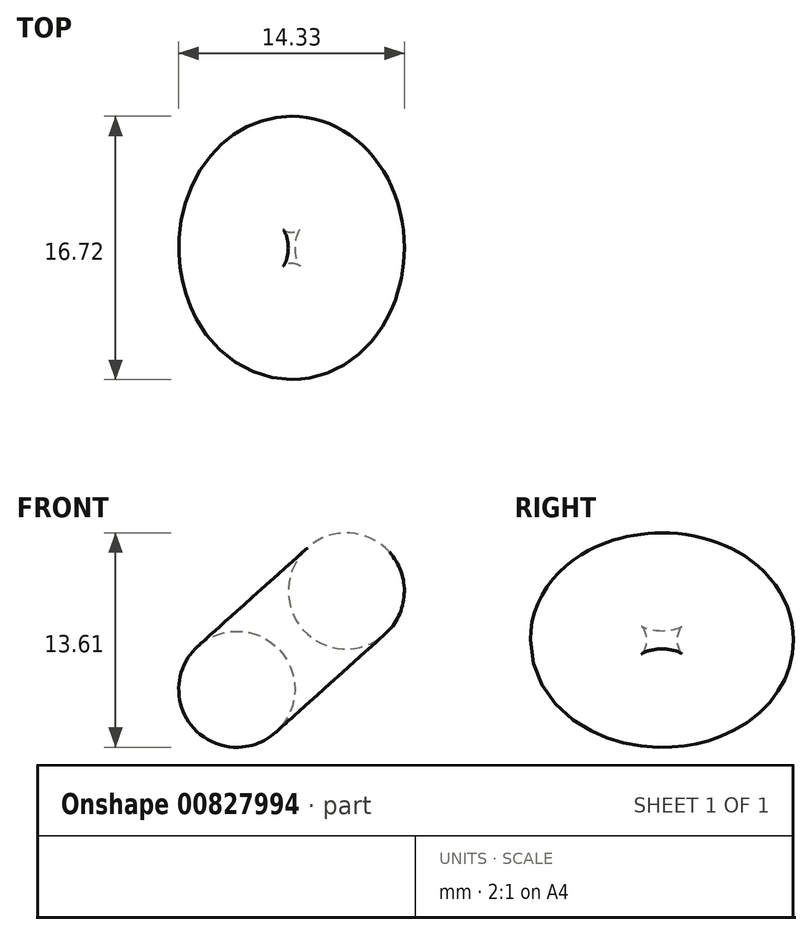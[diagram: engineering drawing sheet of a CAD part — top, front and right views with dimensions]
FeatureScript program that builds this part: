
annotation { "Feature Type Name" : "Feature", "Feature Type Description" : "" }
export const myFeature = defineFeature(function(context is Context, id is Id, definition is map)
    precondition{}
    {
        {
            var Q0;
            Q0=qCreatedBy(makeId("Front.planeOp"),FACE);
            var sketch = newSketch(context, id + "F0", { "sketchPlane" : qUnion([Q0])});
            skLineSegment(sketch, "E0", {"start": v(-4.46, 5.32) * mm, "end": v(5.61, -5.9) * mm});
            skCircle(sketch, "E1", {"center": v(-53.1, 52.52) * mm, "radius": 3.69 * mm});
            skSolve(sketch);
        }
        {
            var Q0;
            Q0=makeQuery(id+"F0.imprint","IMPRINT",FACE,{"disambiguationData":[TD([[makeQuery(id+"F0.imprint","IMPRINT",EDGE,{"derivedFrom":sQuery(id+"F0.wireOp",EDGE,"E1")}),1.0]])]});
            var Q1;
            Q1=sQuery(id+"F0.wireOp",EDGE,"E0");
            revolve(context, id + "F1", {"surfaceOperationType" : NewSurfaceOperationType.NEW, "entities" : qUnion([Q0]), "axis" : qUnion([Q1]), "revolveType" : RevolveType.FULL});
        }
    });
